# Revit family: Shower-Valve_Trim-KOHLER-MODULO-K-72806T_1
name_source: partatom
category: Plumbing Fixtures
revit_build: Autodesk Revit 2017 (Build: 20160225_1515(x64)
units: mm (PartAtom-declared; Revit-internal decimal feet)

## family parameters
Cut with Voids When Loaded = No
Host = Face
OmniClass Number = 23.31.25.00
OmniClass Title = Toilet and Bath Specialties
Part Type = Normal
Room Calculation Point = No
Round Connector Dimension = Use Diameter
Shared = No

## types (6) — shared parameters
ADA Compliant = No
Assembly Code = D2010700
CW Connection = Yes
Cold Water Inlet = Cold Water Inlet
Date Modified = 10/05/2020
Default Elevation = 42"
Description = Smart with round in-wall shower spool and classic panel (Philfas handle)
Drain Included = No
Flow Rate = 0 GPM
HW Connection = Yes
Height = 7 1/16"
Hot Water Inlet = Hot Water Inlet
Length = 4 3/16"
Manufacturer = KOHLER Co.
Master Format 2014 = 22 42 23
Master Format 2014 Name = Residential Showers
Material = Premium Metal Construction
Pressure = 11.60 psi
Product Name = MODULO
Tempered Water Outlet = Tempered Water Outlet
URL = http://www.kohler.com.cn
Vent Connection = No
Waste Connection = No
Waste Water Outlet = Waste Water Outlet
WaterSense Certified = No
Width = 7 1/16"

## per-type parameters (varying)
| type | Finish | Model | Product Documentation Link | Product Page URL | Type |
| 4,CP-Polished Chrome | Kohler-Metal-CP-Polished_Chrome | K-72806T-4-CP |  |  | 1 |
| B4,AF-Flange Gold | Kohler-Metal-AF-Vibrant_French_Gold | K-72806T-B4-AF | https://files.kohler.com.cn | https://www.kohler.com.cn | 3 |
| B4,BN-Brushed Nickel | Kohler-Metal-BN-Vibrant_Brushed_Nickel | K-72806T-B4-BN | https://files.kohler.com.cn | https://www.kohler.com.cn | 4 |
| B4,BV-Roman Copper | Kohler-Metal-BV-Brushed_Bronze | K-72806T-B4-BV | https://files.kohler.com.cn | https://www.kohler.com.cn | 5 |
| B4,SN-Champagne Gold | Kohler-Metal-SN-Vibrant_Polished_Nickel | K-72806-B4-SN | https://files.kohler.com.cn | https://www.kohler.com.cn | 6 |
| B4,CP-Polished Chrome | Kohler-Metal-CP-Polished_Chrome | K-72806T-B4-CP | https://files.kohler.com.cn | https://www.kohler.com.cn | 2 |

## geometry (parser evidence)
native form markers: Sweep x6
no freeform markers — native parametric forms only
